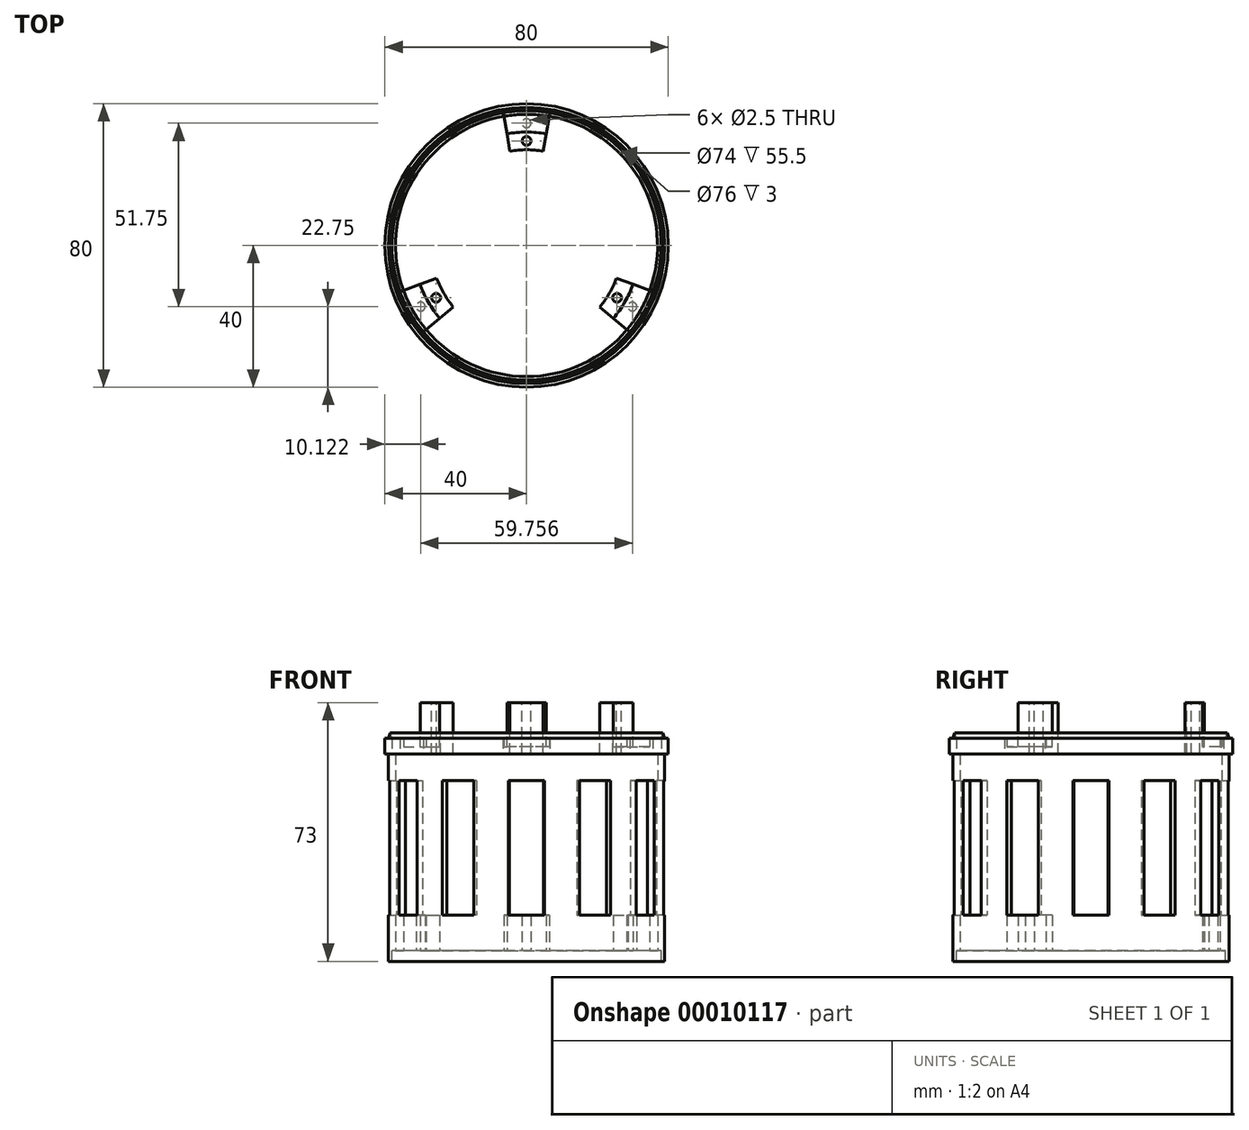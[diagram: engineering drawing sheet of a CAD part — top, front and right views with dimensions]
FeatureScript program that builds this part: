
annotation { "Feature Type Name" : "Feature", "Feature Type Description" : "" }
export const myFeature = defineFeature(function(context is Context, id is Id, definition is map)
    precondition{}
    {
        {
            var Q0;
            Q0=qCreatedBy(makeId("Top.planeOp"),FACE);
            var sketch = newSketch(context, id + "F0", { "sketchPlane" : qUnion([Q0])});
            skCircle(sketch, "E0", {"center": v(0, 0) * mm, "radius": 39 * mm});
            skSolve(sketch);
        }
        {
            var Q0;
            Q0=makeQuery(id+"F0.imprint","IMPRINT",FACE,{"disambiguationData":[TD([[makeQuery(id+"F0.imprint","IMPRINT",EDGE,{"derivedFrom":sQuery(id+"F0.wireOp",EDGE,"E0")}),1.0]])]});
            extrude(context, id + "F1", {"entities" : qUnion([Q0]), "depth" : 3 * mm});
        }
        {
            var Q0;
            Q0=makeQuery(id+"F1.opExtrude","CAP_FACE",FACE,{"disambiguationData":[OSD([sQuery(id+"F0.wireOp",EDGE,"E0")])],"isStart":false});
            var sketch = newSketch(context, id + "F2", { "sketchPlane" : qUnion([Q0])});
            skCircle(sketch, "E1", {"center": v(0, 0) * mm, "radius": 39 * mm});
            skCircle(sketch, "E2", {"center": v(0, 0) * mm, "radius": 37 * mm});
            skSolve(sketch);
        }
        {
            var Q0;
            Q0=makeQuery(id+"F2.imprint","IMPRINT",FACE,{"disambiguationData":[TD([[makeQuery(id+"F2.imprint","IMPRINT",EDGE,{"derivedFrom":sQuery(id+"F2.wireOp",EDGE,"E1")}),1.0]])]});
            extrude(context, id + "F3", {"entities" : qUnion([Q0]), "operationType" : NewBodyOperationType.ADD, "depth" : 60 * mm});
        }
        {
            var Q0;
            Q0=qCreatedBy(makeId("Front.planeOp"),FACE);
            var sketch = newSketch(context, id + "F4", { "sketchPlane" : qUnion([Q0])});
            skLineSegment(sketch, "E3", {"start": v(-37, 60.5) * mm, "end": v(-32, 60.5) * mm});
            skLineSegment(sketch, "E4", {"start": v(-32, 60.5) * mm, "end": v(-32, 73) * mm});
            skLineSegment(sketch, "E5", {"start": v(-40, 63) * mm, "end": v(-39, 63) * mm});
            skLineSegment(sketch, "E6", {"start": v(-39, 63) * mm, "end": v(-38.5, 64.5) * mm});
            skLineSegment(sketch, "E7", {"start": v(-38.5, 64.5) * mm, "end": v(-38, 63) * mm});
            skLineSegment(sketch, "E8", {"start": v(-38.5, 64.5) * mm, "end": v(-38.5, 63) * mm, "construction": true});
            skLineSegment(sketch, "E9", {"start": v(-40, 63) * mm, "end": v(-40, 58.5) * mm});
            skLineSegment(sketch, "E10", {"start": v(-40, 58.5) * mm, "end": v(-27, 58.5) * mm});
            skLineSegment(sketch, "E11", {"start": v(-27, 58.5) * mm, "end": v(-27, 73) * mm});
            skLineSegment(sketch, "E12", {"start": v(-27, 73) * mm, "end": v(-32, 73) * mm});
            skLineSegment(sketch, "E13", {"start": v(-39, 63) * mm, "end": v(-38.5, 63) * mm, "construction": true});
            skLineSegment(sketch, "E14", {"start": v(-38, 63) * mm, "end": v(-37, 63) * mm});
            skLineSegment(sketch, "E15", {"start": v(-37, 60.5) * mm, "end": v(-37, 63) * mm});
            skSolve(sketch);
        }
        {
            var Q0;
            Q0 = qSketchRegion(id + "F4", true);
            var Q1;
            Q1=makeQuery(id+"F3.opExtrude","CAP_EDGE",EDGE,{"disambiguationData":[OSD([sQuery(id+"F2.wireOp",EDGE,"E1")])],"isStart":false});
            sweep(context, id + "F5", {"operationType" : NewBodyOperationType.ADD, "profiles" : qUnion([Q0]), "path" : qUnion([Q1])});
        }
        {
            var Q0;
            Q0=makeQuery(id+"F5.opSweep","SWEPT_FACE",FACE,{"disambiguationData":[OSD([sQuery(id+"F2.wireOp",EDGE,"E1"),sQuery(id+"F4.wireOp",EDGE,"E10")])]});
            var sketch = newSketch(context, id + "F6", { "sketchPlane" : qUnion([Q0])});
            skArc(sketch, "E16", {"start": v(6.6, -37.42) * mm, "mid": v(32.9, -19) * mm, "end": v(35.7, 13) * mm});
            skArc(sketch, "E17", {"start": v(1.74, -9.85) * mm, "mid": v(8.66, -5) * mm, "end": v(9.4, 3.42) * mm});
            skLineSegment(sketch, "E18", {"start": v(0, 0) * mm, "end": v(1.74, -9.85) * mm, "construction": true});
            skLineSegment(sketch, "E19", {"start": v(1.74, -9.85) * mm, "end": v(6.6, -37.42) * mm});
            skLineSegment(sketch, "E20", {"start": v(0, 0) * mm, "end": v(-1.74, -9.85) * mm, "construction": true});
            skLineSegment(sketch, "E21", {"start": v(-1.74, -9.85) * mm, "end": v(-6.6, -37.42) * mm});
            skLineSegment(sketch, "E22", {"start": v(0, 0) * mm, "end": v(0, -38) * mm, "construction": true});
            skLineSegment(sketch, "E23", {"start": v(-6.6, -37.42) * mm, "end": v(0, -38) * mm, "construction": true});
            skLineSegment(sketch, "E24", {"start": v(6.6, -37.42) * mm, "end": v(0, -38) * mm, "construction": true});
            skLineSegment(sketch, "E25.1.0", {"start": v(7.66, 6.43) * mm, "end": v(29.1, 24.43) * mm});
            skLineSegment(sketch, "E25.1.1", {"start": v(9.4, 3.42) * mm, "end": v(35.7, 13) * mm});
            skLineSegment(sketch, "E25.2.0", {"start": v(-9.4, 3.42) * mm, "end": v(-35.7, 13) * mm});
            skLineSegment(sketch, "E25.2.1", {"start": v(-7.66, 6.43) * mm, "end": v(-29.1, 24.43) * mm});
            skArc(sketch, "E26.trimOffspring", {"start": v(-35.7, 13) * mm, "mid": v(-32.9, -19) * mm, "end": v(-6.6, -37.42) * mm});
            skArc(sketch, "E27.trimOffspring", {"start": v(-9.4, 3.42) * mm, "mid": v(-8.66, -5) * mm, "end": v(-1.74, -9.85) * mm});
            skArc(sketch, "E28.trimOffspring", {"start": v(29.1, 24.43) * mm, "mid": v(0, 38) * mm, "end": v(-29.1, 24.43) * mm});
            skArc(sketch, "E29.trimOffspring", {"start": v(7.66, 6.43) * mm, "mid": v(0, 10) * mm, "end": v(-7.66, 6.43) * mm});
            skSolve(sketch);
        }
        {
            var Q0;
            Q0 = qSketchRegion(id + "F6", true);
            var Q1;
            Q1=makeQuery(id+"F5.opSweep","SWEPT_FACE",FACE,{"disambiguationData":[OSD([sQuery(id+"F2.wireOp",EDGE,"E1"),sQuery(id+"F4.wireOp",EDGE,"E12")])]});
            extrude(context, id + "F7", {"entities" : qUnion([Q0]), "operationType" : NewBodyOperationType.REMOVE, "endBound" : BoundingType.UP_TO_SURFACE, "oppositeDirection" : true, "endBoundEntityFace" : qUnion([Q1]), "depth" : 25 * mm});
        }
        {
            var Q0;
            {var subQ0=sQuery(id+"F2.wireOp",EDGE,"E1");Q0=makeQuery(id+"F7.boolean.opBoolean","SPLIT",FACE,{"disambiguationData":[TD([makeQuery(id+"F7.opExtrude","SWEPT_FACE",FACE,{"disambiguationData":[OSD([sQuery(id+"F6.wireOp",EDGE,"E25.2.0")])]})])],"derivedFrom":makeQuery(id+"F5.opSweep","SWEPT_FACE",FACE,{"disambiguationData":[OSD([subQ0,sQuery(id+"F4.wireOp",EDGE,"E12")])]})});}
            var sketch = newSketch(context, id + "F8", { "sketchPlane" : qUnion([Q0])});
            skCircle(sketch, "E30", {"center": v(0, 29.5) * mm, "radius": 1.25 * mm});
            skLineSegment(sketch, "E31", {"start": v(0, 32) * mm, "end": v(0, 29.5) * mm, "construction": true});
            skLineSegment(sketch, "E32", {"start": v(0, 27) * mm, "end": v(0, 29.5) * mm, "construction": true});
            skCircle(sketch, "E33.1.0", {"center": v(-25.55, -14.75) * mm, "radius": 1.25 * mm});
            skCircle(sketch, "E33.2.0", {"center": v(25.55, -14.75) * mm, "radius": 1.25 * mm});
            skPoint(sketch, "E33.center", {"position": v(0, 0) * mm});
            skSolve(sketch);
        }
        {
            var Q0;
            Q0 = qSketchRegion(id + "F8", true);
            extrude(context, id + "F9", {"entities" : qUnion([Q0]), "operationType" : NewBodyOperationType.REMOVE, "endBound" : BoundingType.UP_TO_NEXT, "oppositeDirection" : true, "depth" : 25 * mm});
        }
        {
            var Q0;
            Q0=makeQuery(id+"F1.opExtrude","CAP_FACE",FACE,{"disambiguationData":[OSD([sQuery(id+"F0.wireOp",EDGE,"E0")])],"isStart":false});
            var sketch = newSketch(context, id + "F10", { "sketchPlane" : qUnion([Q0])});
            skLineSegment(sketch, "E34", {"start": v(-6.42, 36.44) * mm, "end": v(-5.56, 31.51) * mm});
            skLineSegment(sketch, "E35", {"start": v(5.56, 31.51) * mm, "end": v(6.42, 36.44) * mm});
            skArc(sketch, "E36", {"start": v(6.42, 36.44) * mm, "mid": v(0, 37) * mm, "end": v(-6.42, 36.44) * mm});
            skLineSegment(sketch, "E37", {"start": v(-5.56, 31.51) * mm, "end": v(0, 0) * mm, "construction": true});
            skLineSegment(sketch, "E38", {"start": v(5.56, 31.51) * mm, "end": v(0, 0) * mm, "construction": true});
            skArc(sketch, "E39", {"start": v(5.56, 31.51) * mm, "mid": v(0, 32) * mm, "end": v(-5.56, 31.51) * mm});
            skLineSegment(sketch, "E40", {"start": v(0, 0) * mm, "end": v(0, 32) * mm, "construction": true});
            skLineSegment(sketch, "E41", {"start": v(0, 32) * mm, "end": v(0, 34.5) * mm, "construction": true});
            skLineSegment(sketch, "E42", {"start": v(0, 34.5) * mm, "end": v(0, 37) * mm, "construction": true});
            skCircle(sketch, "E43", {"center": v(0, 34.5) * mm, "radius": 1.25 * mm});
            skArc(sketch, "E44.1.0", {"start": v(-30.07, -10.94) * mm, "mid": v(-27.71, -16) * mm, "end": v(-24.51, -20.57) * mm});
            skCircle(sketch, "E44.1.1", {"center": v(-29.88, -17.25) * mm, "radius": 1.25 * mm});
            skLineSegment(sketch, "E44.1.2", {"start": v(-28.34, -23.78) * mm, "end": v(-24.51, -20.57) * mm});
            skArc(sketch, "E44.1.3", {"start": v(-34.77, -12.65) * mm, "mid": v(-32.04, -18.5) * mm, "end": v(-28.34, -23.78) * mm});
            skLineSegment(sketch, "E44.1.4", {"start": v(-30.07, -10.94) * mm, "end": v(-34.77, -12.65) * mm});
            skArc(sketch, "E44.2.0", {"start": v(24.51, -20.57) * mm, "mid": v(27.71, -16) * mm, "end": v(30.07, -10.94) * mm});
            skCircle(sketch, "E44.2.1", {"center": v(29.88, -17.25) * mm, "radius": 1.25 * mm});
            skLineSegment(sketch, "E44.2.2", {"start": v(34.77, -12.65) * mm, "end": v(30.07, -10.94) * mm});
            skArc(sketch, "E44.2.3", {"start": v(28.34, -23.78) * mm, "mid": v(32.04, -18.5) * mm, "end": v(34.77, -12.65) * mm});
            skLineSegment(sketch, "E44.2.4", {"start": v(24.51, -20.57) * mm, "end": v(28.34, -23.78) * mm});
            skSolve(sketch);
        }
        {
            var Q0;
            Q0 = qSketchRegion(id + "F10", true);
            extrude(context, id + "F11", {"entities" : qUnion([Q0]), "operationType" : NewBodyOperationType.ADD, "depth" : 10 * mm});
        }
        {
            var Q0;
            Q0=makeQuery(id+"F11.boolean.opBoolean","SPLIT",FACE,{"disambiguationData":[TD([makeQuery(id+"F3.opExtrude","SWEPT_FACE",FACE,{"disambiguationData":[OSD([sQuery(id+"F2.wireOp",EDGE,"E2")])]})])],"derivedFrom":makeQuery(id+"F1.opExtrude","CAP_FACE",FACE,{"disambiguationData":[OSD([sQuery(id+"F0.wireOp",EDGE,"E0")])],"isStart":false})});
            var sketch = newSketch(context, id + "F12", { "sketchPlane" : qUnion([Q0])});
            skCircle(sketch, "E45", {"center": v(0, 0) * mm, "radius": 38 * mm});
            skSolve(sketch);
        }
        {
            var Q0;
            Q0 = qSketchRegion(id + "F12", true);
            extrude(context, id + "F13", {"entities" : qUnion([Q0]), "operationType" : NewBodyOperationType.REMOVE, "endBound" : BoundingType.UP_TO_NEXT, "oppositeDirection" : true, "depth" : 25 * mm});
        }
        {
            var Q0;
            Q0=makeQuery(id+"F11.opExtrude","CAP_FACE",FACE,{"disambiguationData":[OSD([sQuery(id+"F10.wireOp",EDGE,"E34"),sQuery(id+"F10.wireOp",EDGE,"E35"),sQuery(id+"F10.wireOp",EDGE,"E36"),sQuery(id+"F10.wireOp",EDGE,"E39"),sQuery(id+"F10.wireOp",EDGE,"E43")])],"isStart":false});
            var sketch = newSketch(context, id + "F14", { "sketchPlane" : qUnion([Q0])});
            skLineSegment(sketch, "E46", {"start": v(0, 0) * mm, "end": v(4.57, 34.7) * mm, "construction": true});
            skLineSegment(sketch, "E47", {"start": v(4.57, 34.7) * mm, "end": v(5.87, 44.62) * mm});
            skLineSegment(sketch, "E48", {"start": v(5.87, 44.62) * mm, "end": v(-5.87, 44.62) * mm});
            skLineSegment(sketch, "E49", {"start": v(-5.87, 44.62) * mm, "end": v(-4.57, 34.7) * mm});
            skLineSegment(sketch, "E50", {"start": v(-4.57, 34.7) * mm, "end": v(0, 0) * mm, "construction": true});
            skLineSegment(sketch, "E51", {"start": v(4.57, 34.7) * mm, "end": v(-4.57, 34.7) * mm});
            skPoint(sketch, "E52.center", {"position": v(0, 0) * mm});
            skLineSegment(sketch, "E53", {"start": v(0, 0) * mm, "end": v(0, 34.7) * mm, "construction": true});
            skLineSegment(sketch, "E54.1.0", {"start": v(-27.4, 35.7) * mm, "end": v(-21.3, 27.77) * mm});
            skLineSegment(sketch, "E54.1.1", {"start": v(-17.22, 41.57) * mm, "end": v(-27.4, 35.7) * mm});
            skLineSegment(sketch, "E54.1.2", {"start": v(-13.4, 32.34) * mm, "end": v(-17.22, 41.57) * mm});
            skLineSegment(sketch, "E54.1.3", {"start": v(-13.4, 32.34) * mm, "end": v(-21.3, 27.77) * mm});
            skLineSegment(sketch, "E54.2.0", {"start": v(-41.57, 17.22) * mm, "end": v(-32.34, 13.4) * mm});
            skLineSegment(sketch, "E54.2.1", {"start": v(-35.7, 27.4) * mm, "end": v(-41.57, 17.22) * mm});
            skLineSegment(sketch, "E54.2.2", {"start": v(-27.77, 21.3) * mm, "end": v(-35.7, 27.4) * mm});
            skLineSegment(sketch, "E54.2.3", {"start": v(-27.77, 21.3) * mm, "end": v(-32.34, 13.4) * mm});
            skLineSegment(sketch, "E54.3.0", {"start": v(-44.62, -5.87) * mm, "end": v(-34.7, -4.57) * mm});
            skLineSegment(sketch, "E54.3.1", {"start": v(-44.62, 5.87) * mm, "end": v(-44.62, -5.87) * mm});
            skLineSegment(sketch, "E54.3.2", {"start": v(-34.7, 4.57) * mm, "end": v(-44.62, 5.87) * mm});
            skLineSegment(sketch, "E54.3.3", {"start": v(-34.7, 4.57) * mm, "end": v(-34.7, -4.57) * mm});
            skLineSegment(sketch, "E54.4.0", {"start": v(-35.7, -27.4) * mm, "end": v(-27.77, -21.3) * mm});
            skLineSegment(sketch, "E54.4.1", {"start": v(-41.57, -17.22) * mm, "end": v(-35.7, -27.4) * mm});
            skLineSegment(sketch, "E54.4.2", {"start": v(-32.34, -13.4) * mm, "end": v(-41.57, -17.22) * mm});
            skLineSegment(sketch, "E54.4.3", {"start": v(-32.34, -13.4) * mm, "end": v(-27.77, -21.3) * mm});
            skLineSegment(sketch, "E54.5.0", {"start": v(-17.22, -41.57) * mm, "end": v(-13.4, -32.34) * mm});
            skLineSegment(sketch, "E54.5.1", {"start": v(-27.4, -35.7) * mm, "end": v(-17.22, -41.57) * mm});
            skLineSegment(sketch, "E54.5.2", {"start": v(-21.3, -27.77) * mm, "end": v(-27.4, -35.7) * mm});
            skLineSegment(sketch, "E54.5.3", {"start": v(-21.3, -27.77) * mm, "end": v(-13.4, -32.34) * mm});
            skLineSegment(sketch, "E55.2.6.0", {"start": v(5.87, -44.62) * mm, "end": v(4.57, -34.7) * mm});
            skLineSegment(sketch, "E55.3.6.0", {"start": v(-5.87, -44.62) * mm, "end": v(5.87, -44.62) * mm});
            skLineSegment(sketch, "E55.6.6.0", {"start": v(-4.57, -34.7) * mm, "end": v(-5.87, -44.62) * mm});
            skLineSegment(sketch, "E55.9.6.0", {"start": v(-4.57, -34.7) * mm, "end": v(4.57, -34.7) * mm});
            skLineSegment(sketch, "E55.2.7.0", {"start": v(27.4, -35.7) * mm, "end": v(21.3, -27.77) * mm});
            skLineSegment(sketch, "E55.3.7.0", {"start": v(17.22, -41.57) * mm, "end": v(27.4, -35.7) * mm});
            skLineSegment(sketch, "E55.6.7.0", {"start": v(13.4, -32.34) * mm, "end": v(17.22, -41.57) * mm});
            skLineSegment(sketch, "E55.9.7.0", {"start": v(13.4, -32.34) * mm, "end": v(21.3, -27.77) * mm});
            skLineSegment(sketch, "E55.2.8.0", {"start": v(41.57, -17.22) * mm, "end": v(32.34, -13.4) * mm});
            skLineSegment(sketch, "E55.3.8.0", {"start": v(35.7, -27.4) * mm, "end": v(41.57, -17.22) * mm});
            skLineSegment(sketch, "E55.6.8.0", {"start": v(27.77, -21.3) * mm, "end": v(35.7, -27.4) * mm});
            skLineSegment(sketch, "E55.9.8.0", {"start": v(27.77, -21.3) * mm, "end": v(32.34, -13.4) * mm});
            skLineSegment(sketch, "E55.2.9.0", {"start": v(44.62, 5.87) * mm, "end": v(34.7, 4.57) * mm});
            skLineSegment(sketch, "E55.3.9.0", {"start": v(44.62, -5.87) * mm, "end": v(44.62, 5.87) * mm});
            skLineSegment(sketch, "E55.6.9.0", {"start": v(34.7, -4.57) * mm, "end": v(44.62, -5.87) * mm});
            skLineSegment(sketch, "E55.9.9.0", {"start": v(34.7, -4.57) * mm, "end": v(34.7, 4.57) * mm});
            skLineSegment(sketch, "E55.2.10.0", {"start": v(35.7, 27.4) * mm, "end": v(27.77, 21.3) * mm});
            skLineSegment(sketch, "E55.3.10.0", {"start": v(41.57, 17.22) * mm, "end": v(35.7, 27.4) * mm});
            skLineSegment(sketch, "E55.6.10.0", {"start": v(32.34, 13.4) * mm, "end": v(41.57, 17.22) * mm});
            skLineSegment(sketch, "E55.9.10.0", {"start": v(32.34, 13.4) * mm, "end": v(27.77, 21.3) * mm});
            skLineSegment(sketch, "E55.2.11.0", {"start": v(17.22, 41.57) * mm, "end": v(13.4, 32.34) * mm});
            skLineSegment(sketch, "E55.3.11.0", {"start": v(27.4, 35.7) * mm, "end": v(17.22, 41.57) * mm});
            skLineSegment(sketch, "E55.6.11.0", {"start": v(21.3, 27.77) * mm, "end": v(27.4, 35.7) * mm});
            skLineSegment(sketch, "E55.9.11.0", {"start": v(21.3, 27.77) * mm, "end": v(13.4, 32.34) * mm});
            skSolve(sketch);
        }
        {
            var Q0;
            Q0 = qSketchRegion(id + "F14", true);
            var Q1;
            {var subQ0=sQuery(id+"F2.wireOp",EDGE,"E1");var subQ2=sQuery(id+"F6.wireOp",EDGE,"E25.1.0");Q1=makeQuery(id+"F7.boolean.opBoolean","SPLIT",FACE,{"disambiguationData":[TD([makeQuery(id+"F7.opExtrude","SWEPT_FACE",FACE,{"disambiguationData":[OSD([subQ2])]})])],"derivedFrom":makeQuery(id+"F5.opSweep","SWEPT_FACE",FACE,{"disambiguationData":[OSD([subQ0,sQuery(id+"F4.wireOp",EDGE,"E10")])]})});}
            extrude(context, id + "F15", {"entities" : qUnion([Q0]), "operationType" : NewBodyOperationType.REMOVE, "endBoundEntity" : qUnion([Q1]), "depth" : 38 * mm});
        }
    });
